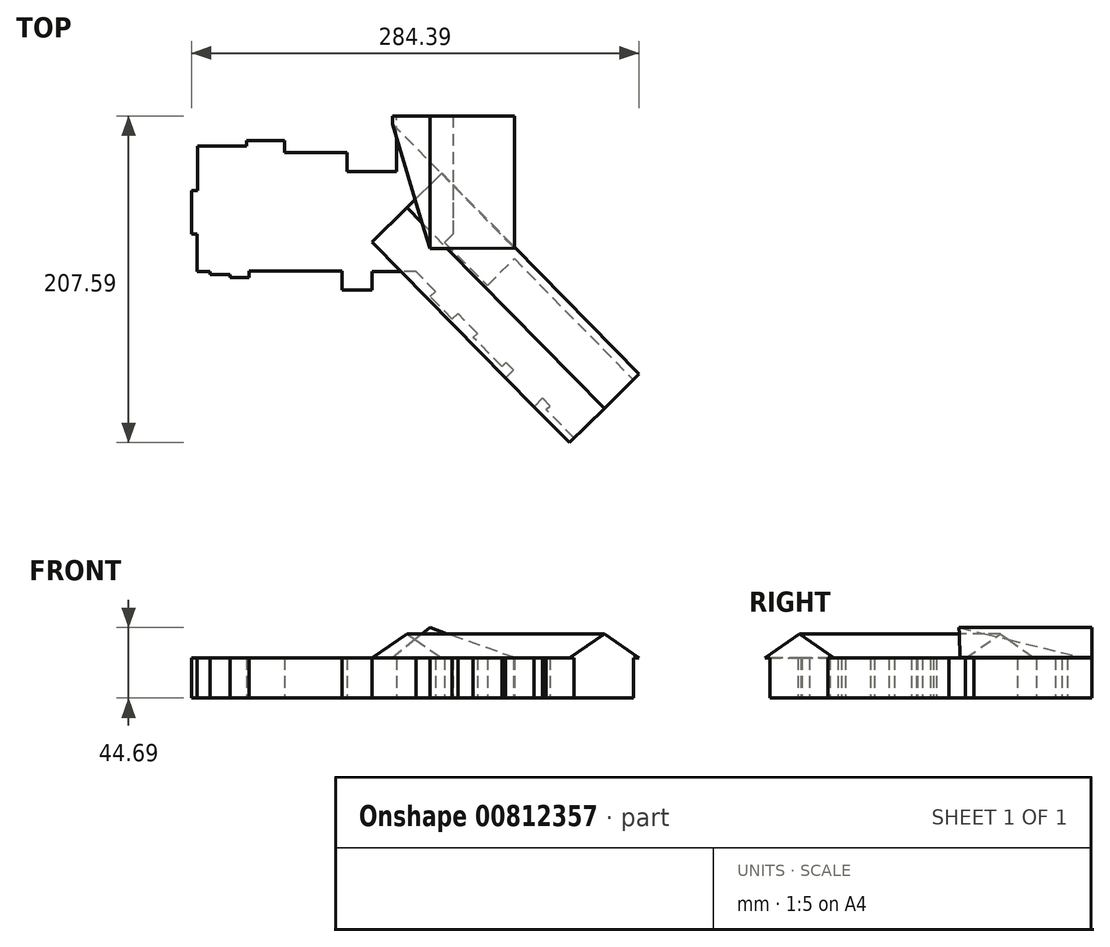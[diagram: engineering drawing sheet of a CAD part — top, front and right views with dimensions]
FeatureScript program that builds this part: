
annotation { "Feature Type Name" : "Feature", "Feature Type Description" : "" }
export const myFeature = defineFeature(function(context is Context, id is Id, definition is map)
    precondition{}
    {
        {
            var Q0;
            Q0=qCreatedBy(makeId("Top.planeOp"),FACE);
            var sketch = newSketch(context, id + "F0", { "sketchPlane" : qUnion([Q0])});
            skLineSegment(sketch, "E0", {"start": v(-116.98, 7.95) * mm, "end": v(-116.98, 36.25) * mm});
            skLineSegment(sketch, "E1", {"start": v(-116.98, 36.25) * mm, "end": v(-85.74, 36.25) * mm});
            skLineSegment(sketch, "E2", {"start": v(-85.74, 36.25) * mm, "end": v(-85.74, 39.75) * mm});
            skLineSegment(sketch, "E3", {"start": v(-85.74, 39.75) * mm, "end": v(-61.55, 39.75) * mm});
            skLineSegment(sketch, "E4", {"start": v(-61.55, 39.75) * mm, "end": v(-61.55, 32.28) * mm});
            skLineSegment(sketch, "E5", {"start": v(-61.55, 32.28) * mm, "end": v(-21.84, 32.28) * mm});
            skLineSegment(sketch, "E6", {"start": v(-21.84, 32.28) * mm, "end": v(-21.84, 20.2) * mm});
            skLineSegment(sketch, "E7", {"start": v(-21.84, 20.2) * mm, "end": v(9.6, 20.2) * mm});
            skLineSegment(sketch, "E8", {"start": v(9.6, 20.2) * mm, "end": v(9.6, 55.44) * mm});
            skLineSegment(sketch, "E9", {"start": v(9.6, 55.44) * mm, "end": v(45.33, 55.44) * mm});
            skLineSegment(sketch, "E10", {"start": v(45.33, 55.44) * mm, "end": v(45.33, -19.57) * mm});
            skLineSegment(sketch, "E11", {"start": v(45.33, -19.57) * mm, "end": v(39.94, -25.04) * mm});
            skLineSegment(sketch, "E12", {"start": v(39.94, -25.04) * mm, "end": v(67.17, -52.2) * mm});
            skLineSegment(sketch, "E13", {"start": v(67.17, -52.2) * mm, "end": v(84.3, -35.34) * mm});
            skLineSegment(sketch, "E14", {"start": v(84.3, -35.34) * mm, "end": v(159.86, -112.19) * mm});
            skLineSegment(sketch, "E15", {"start": v(159.86, -112.19) * mm, "end": v(122.2, -149.2) * mm});
            skLineSegment(sketch, "E16", {"start": v(122.2, -149.2) * mm, "end": v(104.49, -131.18) * mm});
            skLineSegment(sketch, "E17", {"start": v(104.49, -131.18) * mm, "end": v(107.03, -128.69) * mm});
            skLineSegment(sketch, "E18", {"start": v(107.03, -128.69) * mm, "end": v(102.32, -123.9) * mm});
            skLineSegment(sketch, "E19", {"start": v(102.32, -123.9) * mm, "end": v(96.75, -129.39) * mm});
            skLineSegment(sketch, "E20", {"start": v(96.75, -129.39) * mm, "end": v(78.72, -111.05) * mm});
            skLineSegment(sketch, "E21", {"start": v(78.72, -111.05) * mm, "end": v(83.87, -105.99) * mm});
            skLineSegment(sketch, "E22", {"start": v(83.87, -105.99) * mm, "end": v(79.06, -101.1) * mm});
            skLineSegment(sketch, "E23", {"start": v(79.06, -101.1) * mm, "end": v(76.39, -103.73) * mm});
            skLineSegment(sketch, "E24", {"start": v(76.39, -103.73) * mm, "end": v(58.19, -85.21) * mm});
            skLineSegment(sketch, "E25", {"start": v(58.19, -85.21) * mm, "end": v(60.77, -82.67) * mm});
            skLineSegment(sketch, "E26", {"start": v(60.77, -82.67) * mm, "end": v(48.38, -70.06) * mm});
            skLineSegment(sketch, "E27", {"start": v(48.38, -70.06) * mm, "end": v(44.8, -73.58) * mm});
            skLineSegment(sketch, "E28", {"start": v(44.8, -73.58) * mm, "end": v(30.83, -59.36) * mm});
            skLineSegment(sketch, "E29", {"start": v(30.83, -59.36) * mm, "end": v(34.24, -56) * mm});
            skLineSegment(sketch, "E30", {"start": v(34.24, -56) * mm, "end": v(21.73, -43.29) * mm});
            skLineSegment(sketch, "E31", {"start": v(21.73, -43.29) * mm, "end": v(-6.13, -43.29) * mm});
            skLineSegment(sketch, "E32", {"start": v(-6.13, -43.29) * mm, "end": v(-6.13, -55.32) * mm});
            skLineSegment(sketch, "E33", {"start": v(-6.13, -55.32) * mm, "end": v(-25.08, -55.32) * mm});
            skLineSegment(sketch, "E34", {"start": v(-25.08, -55.32) * mm, "end": v(-25.08, -43.27) * mm});
            skLineSegment(sketch, "E35", {"start": v(-25.08, -43.27) * mm, "end": v(-84.32, -43.27) * mm});
            skLineSegment(sketch, "E36", {"start": v(-84.32, -43.27) * mm, "end": v(-84.32, -47.34) * mm});
            skLineSegment(sketch, "E37", {"start": v(-84.32, -47.34) * mm, "end": v(-96.28, -47.34) * mm});
            skLineSegment(sketch, "E38", {"start": v(-96.28, -47.34) * mm, "end": v(-96.28, -45.32) * mm});
            skLineSegment(sketch, "E39", {"start": v(-96.28, -45.32) * mm, "end": v(-108.95, -45.32) * mm});
            skLineSegment(sketch, "E40", {"start": v(-108.95, -45.32) * mm, "end": v(-108.95, -43.41) * mm});
            skLineSegment(sketch, "E41", {"start": v(-108.95, -43.41) * mm, "end": v(-117.04, -43.41) * mm});
            skLineSegment(sketch, "E42", {"start": v(-117.04, -43.41) * mm, "end": v(-117.04, -19.54) * mm});
            skLineSegment(sketch, "E43", {"start": v(-117.04, -19.54) * mm, "end": v(-120.78, -19.54) * mm});
            skLineSegment(sketch, "E44", {"start": v(-120.78, -19.54) * mm, "end": v(-120.78, 7.9) * mm});
            skLineSegment(sketch, "E45", {"start": v(-120.78, 7.9) * mm, "end": v(-116.98, 7.95) * mm});
            skSolve(sketch);
        }
        {
            var Q0;
            Q0 = qSketchRegion(id + "F0", true);
            extrude(context, id + "F1", {"entities" : qUnion([Q0]), "depth" : 25.4 * mm, "offsetDistance" : 25.4 * mm});
        }
        {
            var Q0;
            Q0=makeQuery(id+"F1.opExtrude","SWEPT_FACE",FACE,{"disambiguationData":[OSD([sQuery(id+"F0.wireOp",EDGE,"E15")])]});
            var sketch = newSketch(context, id + "F2", { "sketchPlane" : qUnion([Q0])});
            skLineSegment(sketch, "E46", {"start": v(-21.66, 25.4) * mm, "end": v(9.47, 40.76) * mm});
            skLineSegment(sketch, "E47", {"start": v(9.47, 40.76) * mm, "end": v(40.6, 25.4) * mm});
            skLineSegment(sketch, "E48", {"start": v(40.6, 25.4) * mm, "end": v(-21.66, 25.4) * mm});
            skSolve(sketch);
        }
        {
            var Q0;
            Q0 = qSketchRegion(id + "F2", true);
            var Q1;
            Q1=makeQuery(id+"F1.opExtrude","SWEPT_FACE",FACE,{"disambiguationData":[OSD([sQuery(id+"F0.wireOp",EDGE,"E10")])]});
            var Q2;
            Q2=makeQuery(id+"F1.opExtrude","CAP_VERTEX",VERTEX,{"disambiguationData":[OSD([sQuery(id+"F0.wireOp",EDGE,"E34"),sQuery(id+"F0.wireOp",EDGE,"E35")])],"isStart":false});
            extrude(context, id + "F3", {"entities" : qUnion([Q0]), "operationType" : NewBodyOperationType.ADD, "endBound" : BoundingType.UP_TO_VERTEX, "oppositeDirection" : true, "depth" : 25.4 * mm, "endBoundEntityFace" : qUnion([Q1]), "endBoundEntityVertex" : qUnion([Q2]), "offsetDistance" : 25.4 * mm});
        }
        {
            var Q0;
            Q0=makeQuery(id+"F1.opExtrude","SWEPT_FACE",FACE,{"disambiguationData":[OSD([sQuery(id+"F0.wireOp",EDGE,"E9")])]});
            var sketch = newSketch(context, id + "F4", { "sketchPlane" : qUnion([Q0])});
            skLineSegment(sketch, "E49", {"start": v(-84.34, 25.65) * mm, "end": v(-30.6, 44.69) * mm});
            skLineSegment(sketch, "E50", {"start": v(-30.6, 44.69) * mm, "end": v(-6.92, 25.58) * mm});
            skLineSegment(sketch, "E51", {"start": v(-6.92, 25.58) * mm, "end": v(-84.34, 25.65) * mm});
            skSolve(sketch);
        }
        {
            var Q0;
            Q0 = qSketchRegion(id + "F4", true);
            var Q1;
            Q1=makeQuery(id+"F3.opExtrude","SWEPT_FACE",FACE,{"disambiguationData":[OSD([sQuery(id+"F2.wireOp",EDGE,"E47")])]});
            var Q2;
            Q2=makeQuery(id+"F3.opExtrude","CAP_VERTEX",VERTEX,{"disambiguationData":[OSD([sQuery(id+"F2.wireOp",EDGE,"E46"),sQuery(id+"F2.wireOp",EDGE,"E47")])],"isStart":false});
            extrude(context, id + "F5", {"entities" : qUnion([Q0]), "operationType" : NewBodyOperationType.ADD, "endBound" : BoundingType.UP_TO_SURFACE, "oppositeDirection" : true, "depth" : 83.82 * mm, "endBoundEntityFace" : qUnion([Q1]), "endBoundEntityVertex" : qUnion([Q2]), "offsetDistance" : 25.4 * mm});
        }
    });
